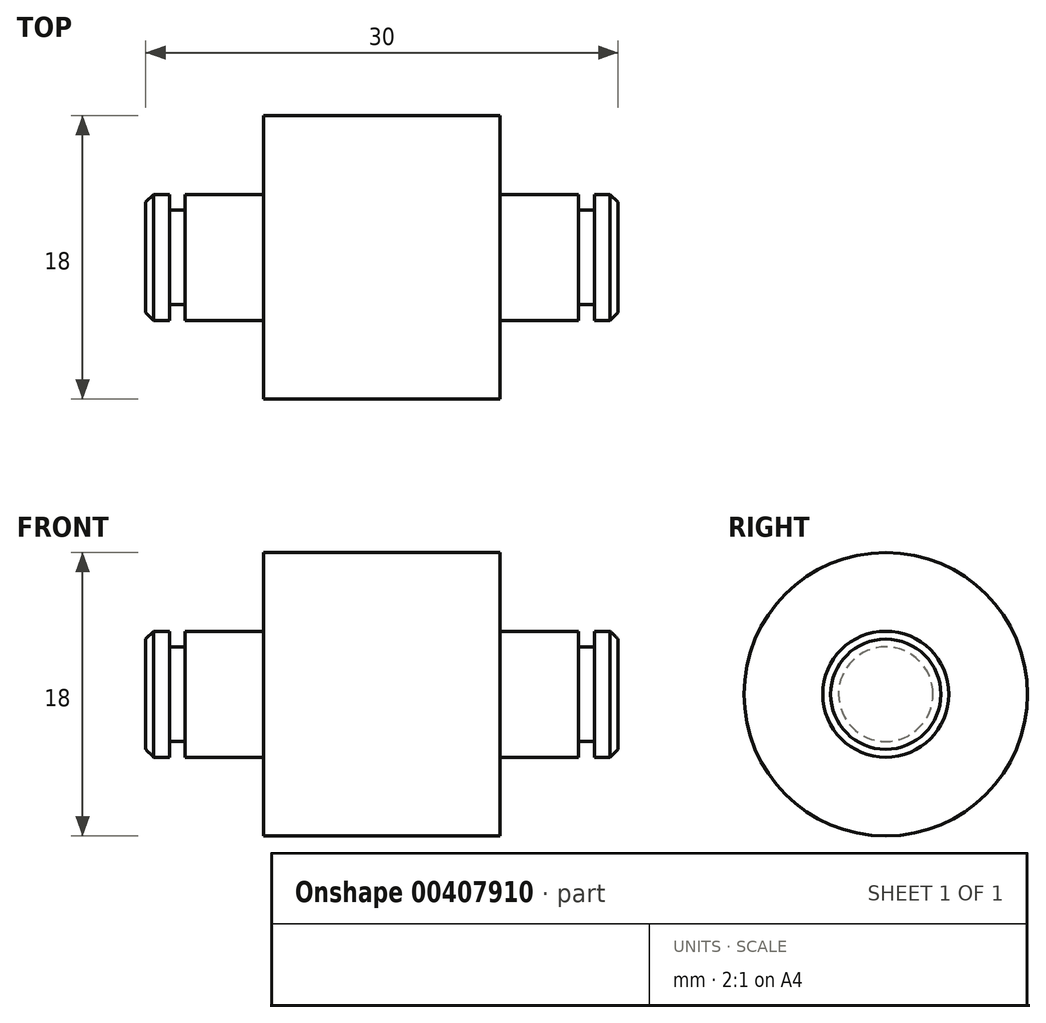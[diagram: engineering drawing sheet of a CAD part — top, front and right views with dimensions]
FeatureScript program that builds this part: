
annotation { "Feature Type Name" : "Feature", "Feature Type Description" : "" }
export const myFeature = defineFeature(function(context is Context, id is Id, definition is map)
    precondition{}
    {
        {
            var Q0;
            Q0=qCreatedBy(makeId("Front.planeOp"),FACE);
            var sketch = newSketch(context, id + "F0", { "sketchPlane" : qUnion([Q0])});
            skLineSegment(sketch, "E0", {"start": v(0, 0) * mm, "end": v(0, 4) * mm});
            skLineSegment(sketch, "E1", {"start": v(-7.5, 4) * mm, "end": v(-7.5, 9) * mm});
            skLineSegment(sketch, "E2", {"start": v(-7.5, 9) * mm, "end": v(-22.5, 9) * mm});
            skLineSegment(sketch, "E3", {"start": v(-22.5, 9) * mm, "end": v(-22.5, 4) * mm});
            skLineSegment(sketch, "E4", {"start": v(-22.5, 4) * mm, "end": v(-27.5, 4) * mm});
            skLineSegment(sketch, "E5", {"start": v(-27.5, 4) * mm, "end": v(-27.5, 3) * mm});
            skLineSegment(sketch, "E6", {"start": v(-27.5, 3) * mm, "end": v(-28.5, 3) * mm});
            skLineSegment(sketch, "E7", {"start": v(-28.5, 3) * mm, "end": v(-28.5, 4) * mm});
            skLineSegment(sketch, "E8", {"start": v(-28.5, 4) * mm, "end": v(-30, 4) * mm});
            skLineSegment(sketch, "E9", {"start": v(-30, 4) * mm, "end": v(-30, 0) * mm});
            skLineSegment(sketch, "E10", {"start": v(-30, 0) * mm, "end": v(0, 0) * mm});
            skLineSegment(sketch, "E11", {"start": v(-15, 9) * mm, "end": v(-15, 0) * mm, "construction": true});
            skLineSegment(sketch, "E12", {"start": v(-7.5, 4) * mm, "end": v(-2.5, 4) * mm});
            skLineSegment(sketch, "E13", {"start": v(-2.5, 4) * mm, "end": v(-2.5, 3) * mm});
            skLineSegment(sketch, "E14", {"start": v(-2.5, 3) * mm, "end": v(-1.5, 3) * mm});
            skLineSegment(sketch, "E15", {"start": v(-1.5, 3) * mm, "end": v(-1.5, 4) * mm});
            skLineSegment(sketch, "E16", {"start": v(-1.5, 4) * mm, "end": v(0, 4) * mm});
            skSolve(sketch);
        }
        {
            var Q0;
            Q0=makeQuery(id+"F0.imprint","IMPRINT",FACE,{"disambiguationData":[TD([[makeQuery(id+"F0.imprint","IMPRINT",EDGE,{"derivedFrom":sQuery(id+"F0.wireOp",EDGE,"E0")}),1.0]])]});
            var Q1;
            Q1=sQuery(id+"F0.wireOp",EDGE,"E10");
            revolve(context, id + "F1", {"entities" : qUnion([Q0]), "axis" : qUnion([Q1]), "revolveType" : RevolveType.FULL});
        }
        {
            var Q0;
            Q0=makeQuery(id+"F1.opRevolve","SWEPT_FACE",FACE,{"disambiguationData":[OSD([sQuery(id+"F0.wireOp",EDGE,"E0")])]});
            var Q1;
            Q1=makeQuery(id+"F1.opRevolve","SWEPT_EDGE",EDGE,{"disambiguationData":[OSD([sQuery(id+"F0.wireOp",EDGE,"E8"),sQuery(id+"F0.wireOp",EDGE,"E9")])]});
            chamfer(context, id + "F2", {"entities" : qUnion([Q0, Q1]), "width" : .5 * mm, "tangentPropagation" : true});
        }
    });
